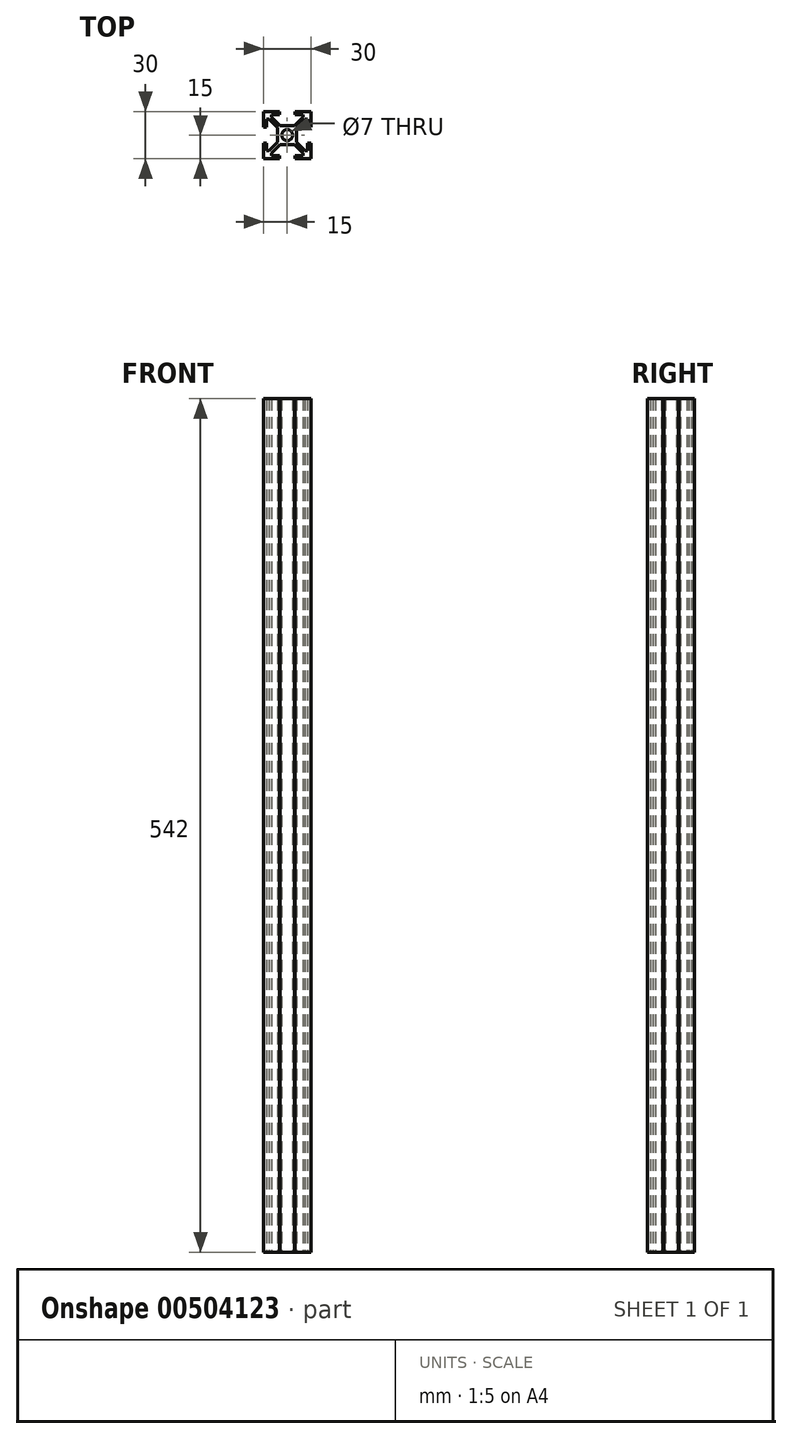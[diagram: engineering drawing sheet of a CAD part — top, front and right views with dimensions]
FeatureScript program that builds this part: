
annotation { "Feature Type Name" : "Feature", "Feature Type Description" : "" }
export const myFeature = defineFeature(function(context is Context, id is Id, definition is map)
    precondition{}
    {
        {
            var Q0;
            Q0=qCreatedBy(makeId("Top.planeOp"),FACE);
            var sketch = newSketch(context, id + "F0", { "sketchPlane" : qUnion([Q0])});
            skCircle(sketch, "E0", {"center": v(0, 0) * mm, "radius": 3.5 * mm});
            skLineSegment(sketch, "E1.bottom", {"start": v(-4.59, 6) * mm, "end": v(4.59, 6) * mm});
            skLineSegment(sketch, "E1.top", {"start": v(-4.59, -6) * mm, "end": v(4.59, -6) * mm});
            skLineSegment(sketch, "E1.left", {"start": v(-6, 4.59) * mm, "end": v(-6, -4.59) * mm});
            skLineSegment(sketch, "E1.right", {"start": v(6, 4.59) * mm, "end": v(6, -4.59) * mm});
            skLineSegment(sketch, "E2", {"start": v(-6, 4.59) * mm, "end": v(-11.41, 10) * mm});
            skLineSegment(sketch, "E3", {"start": v(-4.59, 6) * mm, "end": v(-10, 11.41) * mm});
            skLineSegment(sketch, "E4", {"start": v(-11.41, 10) * mm, "end": v(-13, 10) * mm});
            skLineSegment(sketch, "E5", {"start": v(-13, 10) * mm, "end": v(-13, 5) * mm});
            skLineSegment(sketch, "E6", {"start": v(-13, 5) * mm, "end": v(-15, 5) * mm});
            skLineSegment(sketch, "E7", {"start": v(-15, 5) * mm, "end": v(-15, 15) * mm});
            skLineSegment(sketch, "E8", {"start": v(-15, 15) * mm, "end": v(-5, 15) * mm});
            skLineSegment(sketch, "E9", {"start": v(-5, 15) * mm, "end": v(-5, 13) * mm});
            skLineSegment(sketch, "E10", {"start": v(-5, 13) * mm, "end": v(-10, 13) * mm});
            skLineSegment(sketch, "E11", {"start": v(-10, 13) * mm, "end": v(-10, 11.41) * mm});
            skPoint(sketch, "E12.orphan", {"position": v(-6, 6) * mm});
            skLineSegment(sketch, "E13", {"start": v(0, 0) * mm, "end": v(-5.3, 5.3) * mm, "construction": true});
            skLineSegment(sketch, "E14", {"start": v(-5.3, 5.3) * mm, "end": v(-6, 4.59) * mm, "construction": true});
            skLineSegment(sketch, "E15", {"start": v(-5.3, 5.3) * mm, "end": v(-4.59, 6) * mm, "construction": true});
            skLineSegment(sketch, "E16.2.0", {"start": v(15, 15) * mm, "end": v(15, 5) * mm});
            skLineSegment(sketch, "E16.2.1", {"start": v(5, 15) * mm, "end": v(15, 15) * mm});
            skLineSegment(sketch, "E16.2.2", {"start": v(5, 13) * mm, "end": v(5, 15) * mm});
            skLineSegment(sketch, "E16.2.3", {"start": v(10, 13) * mm, "end": v(5, 13) * mm});
            skLineSegment(sketch, "E16.2.4", {"start": v(10, 11.41) * mm, "end": v(10, 13) * mm});
            skLineSegment(sketch, "E16.2.5", {"start": v(4.59, 6) * mm, "end": v(10, 11.41) * mm});
            skLineSegment(sketch, "E16.2.6", {"start": v(6, 4.59) * mm, "end": v(11.41, 10) * mm});
            skLineSegment(sketch, "E16.2.7", {"start": v(13, 10) * mm, "end": v(11.41, 10) * mm});
            skLineSegment(sketch, "E16.2.8", {"start": v(13, 5) * mm, "end": v(13, 10) * mm});
            skLineSegment(sketch, "E16.2.9", {"start": v(15, 5) * mm, "end": v(13, 5) * mm});
            skLineSegment(sketch, "E16.anchor1", {"start": v(0, 0) * mm, "end": v(-15, 15) * mm, "construction": true});
            skLineSegment(sketch, "E16.anchor2", {"start": v(0, 0) * mm, "end": v(15, 15) * mm, "construction": true});
            skPoint(sketch, "E17.orphan", {"position": v(6, 6) * mm});
            skLineSegment(sketch, "E18.MirrorCS", {"start": v(-13, -5) * mm, "end": v(-15, -5) * mm});
            skLineSegment(sketch, "E19.MirrorCS", {"start": v(-15, -5) * mm, "end": v(-15, -15) * mm});
            skLineSegment(sketch, "E20.MirrorCS", {"start": v(-13, -10) * mm, "end": v(-13, -5) * mm});
            skLineSegment(sketch, "E21.MirrorCS", {"start": v(-11.41, -10) * mm, "end": v(-13, -10) * mm});
            skLineSegment(sketch, "E22.MirrorCS", {"start": v(-6, -4.59) * mm, "end": v(-11.41, -10) * mm});
            skLineSegment(sketch, "E23.MirrorCS", {"start": v(-4.59, -6) * mm, "end": v(-10, -11.41) * mm});
            skLineSegment(sketch, "E24.MirrorCS", {"start": v(-5, -13) * mm, "end": v(-10, -13) * mm});
            skLineSegment(sketch, "E25.MirrorCS", {"start": v(-10, -13) * mm, "end": v(-10, -11.41) * mm});
            skLineSegment(sketch, "E26.MirrorCS", {"start": v(-5, -15) * mm, "end": v(-5, -13) * mm});
            skLineSegment(sketch, "E27.MirrorCS", {"start": v(-15, -15) * mm, "end": v(-5, -15) * mm});
            skLineSegment(sketch, "E28.MirrorCS", {"start": v(5, -13) * mm, "end": v(5, -15) * mm});
            skLineSegment(sketch, "E29.MirrorCS", {"start": v(5, -15) * mm, "end": v(15, -15) * mm});
            skLineSegment(sketch, "E30.MirrorCS", {"start": v(15, -15) * mm, "end": v(15, -5) * mm});
            skLineSegment(sketch, "E31.MirrorCS", {"start": v(15, -5) * mm, "end": v(13, -5) * mm});
            skLineSegment(sketch, "E32.MirrorCS", {"start": v(13, -5) * mm, "end": v(13, -10) * mm});
            skLineSegment(sketch, "E33.MirrorCS", {"start": v(13, -10) * mm, "end": v(11.41, -10) * mm});
            skLineSegment(sketch, "E34.MirrorCS", {"start": v(6, -4.59) * mm, "end": v(11.41, -10) * mm});
            skLineSegment(sketch, "E35.MirrorCS", {"start": v(4.59, -6) * mm, "end": v(10, -11.41) * mm});
            skLineSegment(sketch, "E36.MirrorCS", {"start": v(10, -13) * mm, "end": v(5, -13) * mm});
            skLineSegment(sketch, "E37.MirrorCS", {"start": v(10, -11.41) * mm, "end": v(10, -13) * mm});
            skPoint(sketch, "E38.orphan", {"position": v(-6, -6) * mm});
            skPoint(sketch, "E39.orphan", {"position": v(6, -6) * mm});
            skSolve(sketch);
        }
        {
            var Q0;
            Q0=qSketchRegion(id+"F0",true);
            extrude(context, id + "F1", {"entities" : qUnion([Q0]), "depth" : (592 - 50) * mm});
        }
    });
